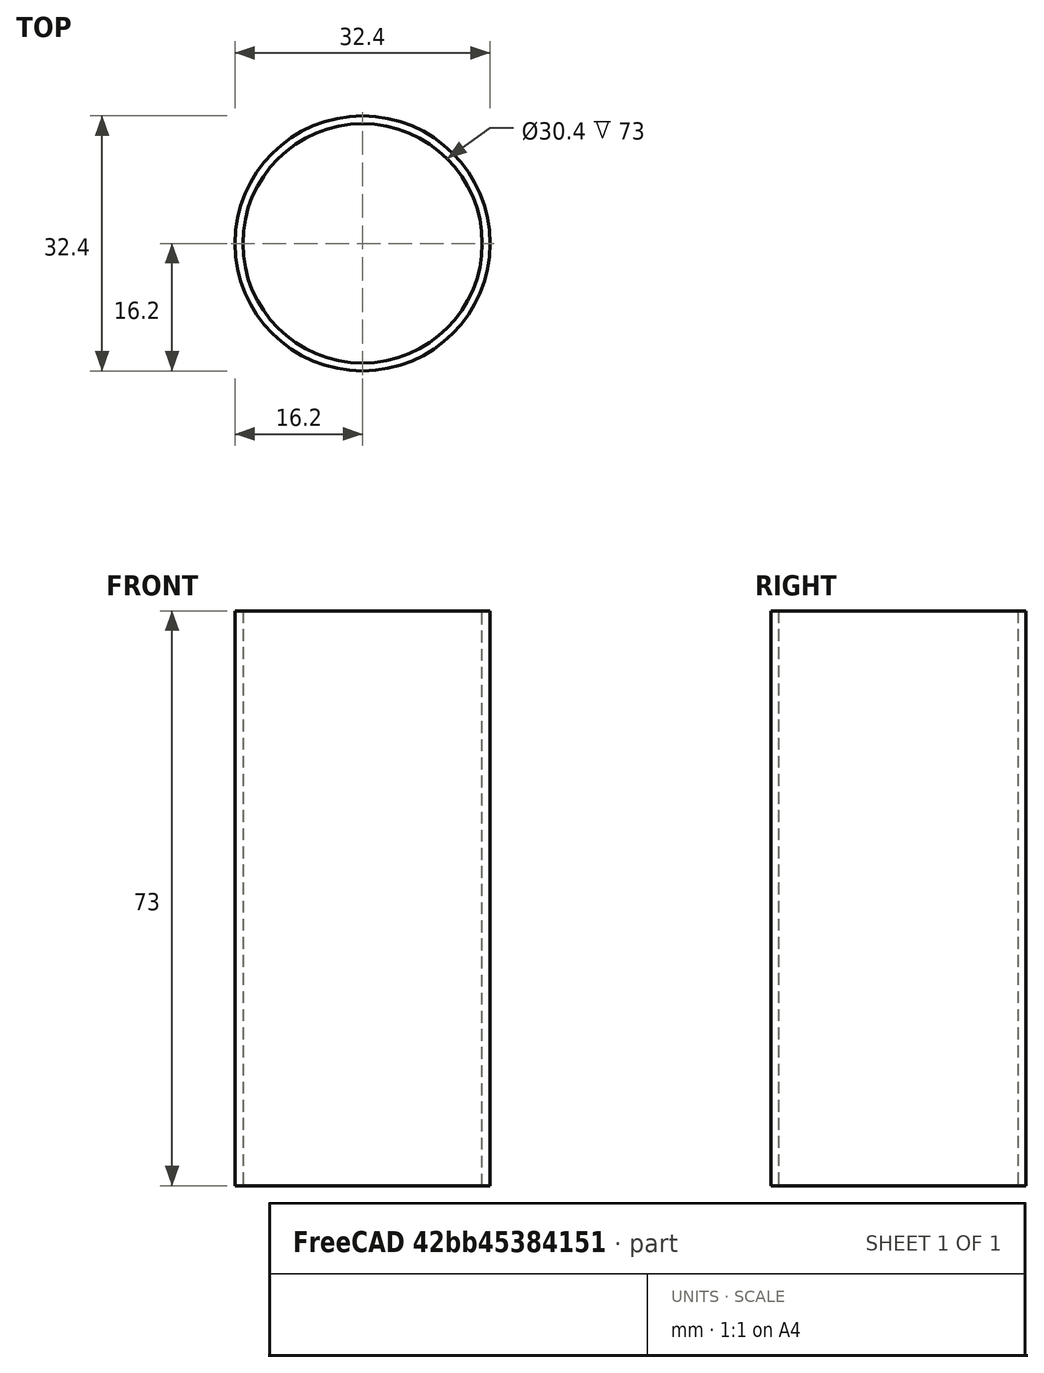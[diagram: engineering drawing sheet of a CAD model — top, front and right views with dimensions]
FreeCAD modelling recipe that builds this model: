
FCSTD DOCUMENT  (FreeCAD 0.19R)
Label: dry box roller
License: All rights reserved
LicenseURL: http://en.wikipedia.org/wiki/All_rights_reserved
objects: Sketcher::SketchObject×1, PartDesign::Pad×1, PartDesign::Body×1
note: 4 computed .brp shape members not serialized (recipe doc carries the construction recipe); baked Part::Feature solids carry a one-line shape summary decoded from their .brp

FEATURE [Sketcher::SketchObject] Sketch
  FullyConstrained = true
  MapMode = 5
  Support = -> [XY_Plane]
  sketch-geometry (2):
    g0: Circle CenterX=0 CenterY=0 CenterZ=0 NormalX=0 NormalY=0 NormalZ=1 AngleXU=0 Radius=15.2
    g1: Circle CenterX=0 CenterY=0 CenterZ=0 NormalX=0 NormalY=0 NormalZ=1 AngleXU=0 Radius=16.2
  constraints (4):
    c: Coincident(g0,g-1)
    c: Coincident(g1,g0)
    c: Diameter(g0) = 30.4
    c: Diameter(g1) = 32.4
FEATURE [PartDesign::Pad] Pad
  Direction = (1,1,1)
  Length = 73
  Length2 = 100
  Profile = -> Sketch
  Type = 0
FEATURE [PartDesign::Body] Body
  Group = -> [Sketch,Pad]
  Origin = -> Origin
  Tip = -> Pad
